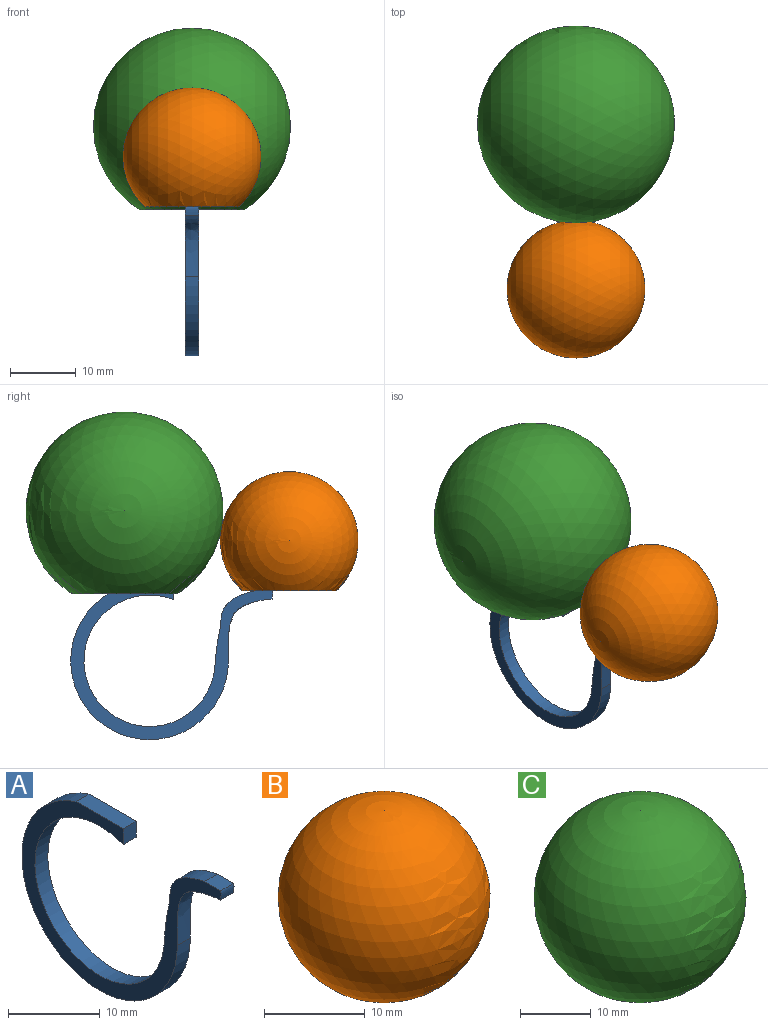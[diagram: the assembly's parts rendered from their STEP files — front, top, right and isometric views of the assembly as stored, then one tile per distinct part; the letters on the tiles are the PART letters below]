
ASSEMBLY  parts=3 mates=1
PART A: 11 faces, bbox 2x30.8x23.4 mm
  f0: extruded ~9.39x6.68mm, area 27.4mm2, adj f1,f8,f9,f10
  f1: cylinder r=12mm len=24mm, axis (-1,0,0), area 105.7mm2, adj f0,f2,f9,f10
  f2: plane 7.28x2mm, normal (0,0,1), area 14.6mm2, adj f1,f3,f9,f10
  f3: plane 2.12x2mm, normal (0,-1,0), area 4.2mm2, adj f2,f4,f9,f10
  f4: cylinder r=10mm len=20mm, axis (-1,0,0), area 101.7mm2, adj f3,f5,f9,f10
  f5: cylinder r=34.14mm len=5.25mm, axis (-1,0,0), area 10.6mm2, adj f4,f6,f9,f10
  f6: extruded ~5.42x5.42mm, area 17.1mm2, adj f5,f7,f9,f10
  f7: plane 2.47x2mm, normal (0,0,1), area 4.9mm2, adj f6,f8,f9,f10
  f8: extruded ~2x1.27mm, area 2.6mm2, adj f0,f7,f9,f10
  f9: plane 30.78x23.44mm, normal (1,0,0), area 132.6mm2, adj f0,f1,f2,f3,f4,f5,f6,f7
  f10: plane 30.78x23.44mm, normal (-1,0,0), area 132.6mm2, adj f0,f1,f2,f3,f4,f5,f6,f7
PART B: 2 faces, bbox 21x21x21 mm
  f0: sphere r=10.5mm, area 1195.4mm2, adj f1
  f1: plane 14.45x14.45mm, normal (1,0,0), area 163.9mm2, adj f0
PART C: 4 faces, bbox 30x30x30 mm
  f0: sphere r=15mm, area 2607mm2, adj f1
  f1: cylinder r=8.04mm len=16.09mm, axis (-1,0,0), area 10.9mm2, adj f0,f2
  f2: plane 16.09x16.09mm, normal (1,0,0), area 74.1mm2, adj f1,f3
  f3: sphere r=14mm, area 2326.3mm2, adj f2
PLACE A t=(-20.31,-6.09,2.8)mm
PLACE B rot(axis=(0.71,0,-0.71),180deg) t=(-19.31,-27.34,21.09)mm
PLACE C rot(axis=(0.71,0,-0.71),180deg) t=(-19.31,-2.28,25.67)mm
MATE fastened B.f1 <-> A.f7  axis (0,0,-1) through (-19.31,-27.34,13.47)mm
